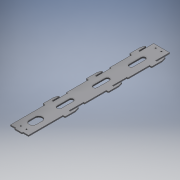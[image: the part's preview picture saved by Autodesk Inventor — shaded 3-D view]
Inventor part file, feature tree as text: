
AUTODESK INVENTOR PART (.ipt)
format: ipt  version: 2017 (Build 210142000, 142)  size: 240,640 bytes
history: native  units: mm
features: sketch x7, extrude x5, hole x2, pattern_linear x1, mirror x1
ambient origin geometry x8: Origin, YZ Plane, XZ Plane, XY Plane, X Axis, Y Axis, Z Axis, Center Point
bodies: Solid1 (feature_tree)
feature tree (16):
  extrude  "Extrusion1"  Depth=50.0mm
  extrude  "Extrusion2"  Depth=20.0mm
  extrude  "Extrusion3"  Depth=120.0mm
  pattern_linear  "Rectangular Pattern1"  Count1=2  [1 undecoded]
  mirror  "Mirror1"
  hole  "Hole1"  [1 undecoded]
  extrude  "Extrusion4"  Depth=3.0mm TaperAngle=0.0deg
  extrude  "Extrusion5"  Depth=2.0mm
  hole  "Hole2"  [1 undecoded]
  sketch  "Sketch1"  dims[d0=394.0mm d1=50.0mm]
  sketch  "Sketch2"  dims[d2=3.0mm d3=0.0mm d4=20.0mm]
  sketch  "Sketch3"  dims[d5=3.0mm d6=0.0mm d7=30.0mm d9=120.0mm d10=20.0mm]
  sketch  "Sketch4"  dims[d11=20.0mm d12=20.0mm]
  sketch  "Sketch5"  dims[d13=6.0mm d14=3.0mm d15=0.0mm]
  sketch  "Sketch6"  dims[d16=2.0mm d17=16.0mm]
  sketch  "Sketch7"  dims[d19=3.2mm d20=6.0mm d21=4.0mm d22=2.0mm d23=90.0deg d24=8.0mm d25=20.594885mm d26=3.0mm d27=0.0mm d28=10.0mm d29=45.0mm d30=3.0mm d31=0.0mm d32=16.0mm d33=17.0mm d34=3.2mm d35=6.0mm d36=4.0mm d37=2.0mm d38=90.0deg d39=8.0mm d40=20.594885mm d41=30.0mm d43=100.0mm d44=10.0mm d46=10.0mm d48=6.0mm d50=20.0mm d51=15.0mm d52=10.0mm d53=14.0mm d54=10.0mm d55=60.0mm d56=20.0mm]
note: 3 required parameter values undecoded (feature->parameter linkage not recoverable at this tier; creation-order binding heuristic only, values carry confidence <= 0.55)
